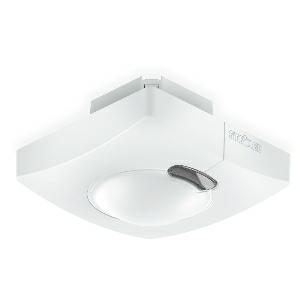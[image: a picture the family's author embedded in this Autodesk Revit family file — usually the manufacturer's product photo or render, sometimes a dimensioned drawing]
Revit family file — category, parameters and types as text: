
# Revit family: hf_3360_057336
name_source: partatom
category: Elektroinstallationen
revit_build: Autodesk Revit 2016 (Build: 20190508_0715(x64)
units: mm (PartAtom-declared; Revit-internal decimal feet)

## family parameters
Basisbauteil = Fläche
Beim Laden mit Abzugskörper schneiden = Nein
Bemaßung runder Anschluss = Durchmesser verwenden
Beschriftungsausrichtung beibehalten = Nein
Gemeinsam genutzt = Nein
Raumberechnungspunkt = Nein
Teiletyp = Normal

## types (1)
- HF 3360
    Apparent Load = 0 VA
    Beschreibung = Type: Motion detectors; Dimensions (L x W x H): 64 x 94 x 94 mm; Mains power supply: 12 – 22,5 V; Power consumption: 0,5 W; Sensor Technology: High frequency; Application, place: Indoors; Application, room: function room / ancillary room, stairwell, WC / washroom, multi-storey / underground car park, Indoors; Installation site: wall, ceiling, corner; Installation: Concealed wiring; HF-system: 5,8 GHz; Electronic scalability: Yes; Mechanical scalability: No; Mounting height: 2,00 – 4,00 m; Optimum mounting height: 2,8 m; Detection: also through glass, wood and stud walls; Detection angle: 360 °; Angle of aperture: 160 °; Sneak-by guard: Yes; Reach, radial: Ø 8 m (50 m²); Reach, tangential: Ø 8 m (50 m²); Twilight setting TEACH: No; Twilight setting: 2 – 1000 lx; Control output, Dali: Addressable/slave; Constant-lighting control: No; Basic light level function: No; With bus coupling: Yes; Settings via: Bus; With remote control: No; IP-rating: IP20; Material: Plastic; Ambient temperature: -20 – 50 °C; Colour: white; Colour, RAL: 9003; Manufacturer's Warranty: 5 years; Version: DALI-2 IPD - concealed, sq.; PU1, EAN: 4007841057336
    Height = 94 mm  [stored 0.308399 ft]
    Hersteller = Steinel
    Length = 64 mm
    ModVariant = Nein
    Modell = 057336
    Mounting Type = Recessed
    Number of Poles = 1
    OnlyDefault = Ja
    Power Factor = 1
    Product Name = HF 3360
    Product group = Sensor-switched indoor light
    ProductGroupID = 30
    Protection Class = Protection class
    Protection Degree = IP 20
    RlxData = <blob elided: 26621 chars, md5=45371711>
    SensorDataFile = {"IESDataFiles":[]}
    Typenbild = produkt1_057336.jpg
    Typenkommentare = Product without accessories
    URL = http://relux.com
    VarID = ---
    Voltage = 0 V
    Vorgabe-Ansicht = 1800 mm
    Weight = 0.00 kg
    Width = 94 mm  [stored 0.308399 ft]

note: [stored X ft] marks values corroborated as IEEE doubles in the binary element streams (Revit-internal decimal feet)

## geometry (parser evidence)
native form markers: Blend x4, Sweep x11
no freeform markers — native parametric forms only
